# Revit family: Automatic air vents with check valve 2630 00 (01)
name_source: partatom
category: Rohrzubehör
units: mm (PartAtom-declared; Revit-internal decimal feet)

## family parameters
Arbeitsebenenbasiert = Nein
Beim Laden mit Abzugskörper schneiden = Nein
Bemaßung runder Anschluss = Durchmesser verwenden
Gemeinsam genutzt = Nein
Immer vertikal = Ja
OmniClass-Nummer = 23.65.55.14
OmniClass-Titel = Valves for Liquid Services
Teiletyp = Normal

## types (1)
- Automatic air vents with check valve 2630 00 (01)
    Backflow preventer housing = machined brass acc. to EN 12165, CW617N 5
    Cover cap = polypropylene, black colour
    D01 = 16.2 mm  [stored 0.0531496 ft]
    D02 = 19.5 mm  [stored 0.0639764 ft]
    D03 = 5.1 mm  [stored 0.0167323 ft]
    D04 = 3.4 mm
    D05 = 0.8 mm
    D06 = 4 mm  [stored 0.0131234 ft]
    D07 = 11.5 mm  [stored 0.0377297 ft]
    External threaded connectors = acc. to ISO 228
    Field of application = HERZ - Air vent is used for venting of the central heating installations.
the air vent should be placed nearby the boiler or at the highest points of installation.
installations must be carried out in such a way that the retention of air bubbles in a certain part of installation is not possible.
before usage, unscrew the polypropylene cover cap on the lid for 2 to 3 turns.
in case of uncontrolled medium leakage, tighten the cover cap.
the air vent must be cleaned or replaced.
we always recommend to use backflow preventer for easy service and replacement of the air vent.
    Float ball = polypropylene
    G = 5 mm  [stored 0.0164042 ft]
    H00 = 59 mm
    H01 = 12 mm  [stored 0.0393701 ft]
    H02 = 9.5 mm  [stored 0.031168 ft]
    H03 = 63 mm
    H04 = 57.9 mm
    H05 = 58 mm  [stored 0.190289 ft]
    H06 = 25.3 mm  [stored 0.0830052 ft]
    H07 = 9.8 mm  [stored 0.0321522 ft]
    H08 = 13.2 mm  [stored 0.0433071 ft]
    Hersteller = Herz-Armaturen GmbH
    Housing = forged brass acc. to EN 12165, CW617N
    L00 = 33.5 mm
    L01 = 9.5 mm  [stored 0.031168 ft]
    L02 = 4.8 mm  [stored 0.015748 ft]
    L03 = 13.5 mm
    L04 = 24 mm  [stored 0.0787402 ft]
    Lid = forged brass acc. to EN 12165, CW617N
    Medium = heating water quality according to ÖNORM H5195 or VDI-Standard 2035.
the use of ethylene or propylene glycol in a mixing ratio 25-50% is allowed.
please refer to manufacturers documentation when using ethylene glycol products for frost and corrosion protection.
the HERZ air vent is not suitable for usage of aggressive medium (such as: acids, alkalis, combustible and explosive gases..) because it can damage the sealing components.
    R01 = 2 mm  [stored 0.00656168 ft]
    S01 = 59 mm
    S02 = 24.5 mm
    S03 = 11 mm  [stored 0.0360892 ft]
    S04 = 21 mm  [stored 0.0688976 ft]
    S05 = 25.3 mm  [stored 0.0830052 ft]
    SCRNCODE = 05;14;01
    SCRNSEQ = AWI;AWI_TYP="1013";1
    SW = 10.5 mm  [stored 0.0344488 ft]
    Sealing = NBR
    URL = www.herzvalves.com
    max. Operating pressure = 800000.0 Pa
    max. Operating temperature = 110 °C
    max. Structual pressure = 1200000.0 Pa
    min. Operating temperature = 0 °C

note: [stored X ft] marks values corroborated as IEEE doubles in the binary element streams (Revit-internal decimal feet)
